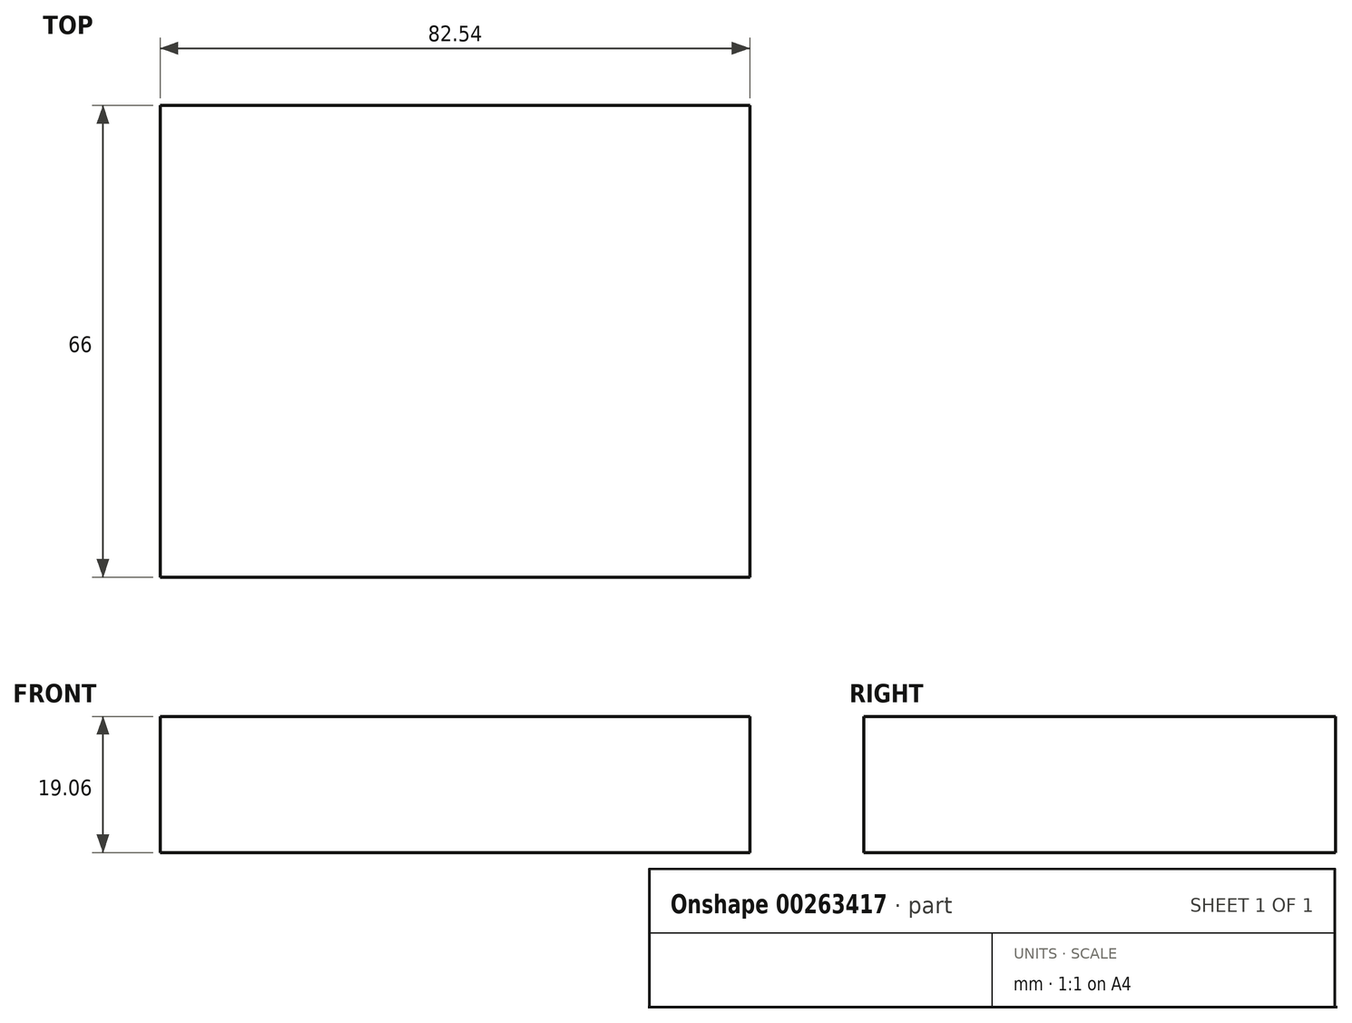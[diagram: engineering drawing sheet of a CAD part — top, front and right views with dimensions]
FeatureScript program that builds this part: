
annotation { "Feature Type Name" : "Feature", "Feature Type Description" : "" }
export const myFeature = defineFeature(function(context is Context, id is Id, definition is map)
    precondition{}
    {
        {
            var Q0;
            Q0=qCreatedBy(makeId("Front.planeOp"),FACE);
            var sketch = newSketch(context, id + "F0", { "sketchPlane" : qUnion([Q0])});
            skLineSegment(sketch, "E0.bottom", {"start": v(-41.28, 9.52) * mm, "end": v(41.27, 9.53) * mm});
            skLineSegment(sketch, "E0.top", {"start": v(-41.27, -9.53) * mm, "end": v(41.28, -9.53) * mm});
            skLineSegment(sketch, "E0.left", {"start": v(-41.27, 9.52) * mm, "end": v(-41.27, -9.53) * mm});
            skLineSegment(sketch, "E0.right", {"start": v(41.27, 9.53) * mm, "end": v(41.28, -9.52) * mm});
            skPoint(sketch, "E0.middle", {"position": v(0, 0) * mm});
            skLineSegment(sketch, "E1.bottom", {"start": v(60.32, 38.1) * mm, "end": v(111.12, 38.1) * mm});
            skLineSegment(sketch, "E1.top", {"start": v(60.32, 66.68) * mm, "end": v(111.12, 66.68) * mm});
            skLineSegment(sketch, "E1.left", {"start": v(60.32, 38.1) * mm, "end": v(60.32, 66.68) * mm});
            skLineSegment(sketch, "E1.right", {"start": v(111.12, 38.1) * mm, "end": v(111.12, 66.68) * mm});
            skPoint(sketch, "E1.middle", {"position": v(85.72, 52.39) * mm});
            skLineSegment(sketch, "E2", {"start": v(41.27, 9.53) * mm, "end": v(41.27, 28.67) * mm});
            skArc(sketch, "E3", {"start": v(41.27, 28.67) * mm, "mid": v(45.92, 39.9) * mm, "end": v(57.15, 44.54) * mm});
            skLineSegment(sketch, "E4", {"start": v(57.15, 44.54) * mm, "end": v(103.38, 44.54) * mm});
            skArc(sketch, "E5.0", {"start": v(22.22, 28.67) * mm, "mid": v(27.75, 47.52) * mm, "end": v(42.57, 60.4) * mm});
            skLineSegment(sketch, "E5.1", {"start": v(22.22, 9.53) * mm, "end": v(22.22, 28.67) * mm});
            skLineSegment(sketch, "E6", {"start": v(103.38, 38.1) * mm, "end": v(103.38, 66.68) * mm});
            skLineSegment(sketch, "E7", {"start": v(42.57, 60.4) * mm, "end": v(103.38, 60.4) * mm});
            skFitSpline(sketch, "E8", {"points": [v(-41.28, 9.52) * mm, v(42.57, 60.4) * mm], "startDerivative": vector(94.82, 72.69) * mm, "endDerivative": vector(120.93, -1) * mm});
            skSolve(sketch);
        }
        {
            var Q0;
            Q0=makeQuery(id+"F0.imprint","IMPRINT",FACE,{"disambiguationData":[TD([[makeQuery(id+"F0.imprint","IMPRINT",EDGE,{"derivedFrom":sQuery(id+"F0.wireOp",EDGE,"E0.top")}),1.0]])]});
            extrude(context, id + "F1", {"entities" : qUnion([Q0]), "depth" : 66 * mm});
        }
    });
